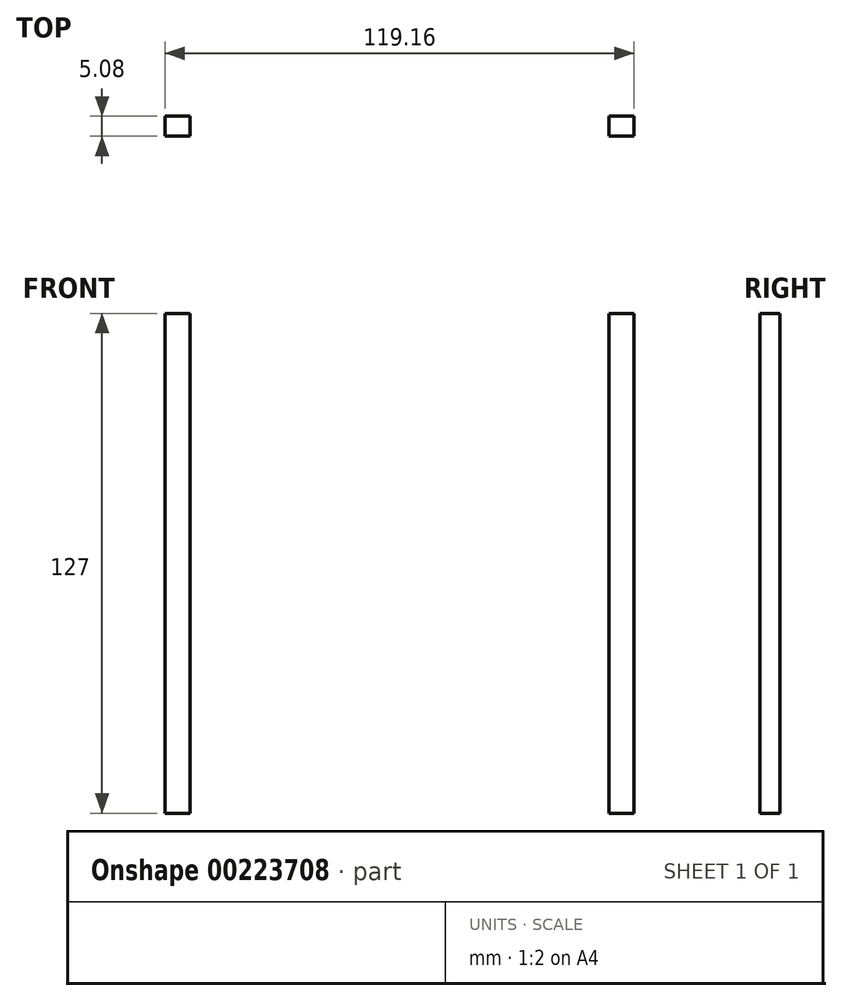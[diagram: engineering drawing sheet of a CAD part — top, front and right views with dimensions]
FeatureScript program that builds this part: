
annotation { "Feature Type Name" : "Feature", "Feature Type Description" : "" }
export const myFeature = defineFeature(function(context is Context, id is Id, definition is map)
    precondition{}
    {
        {
            var Q0;
            Q0=qCreatedBy(makeId("Front.planeOp"),FACE);
            var sketch = newSketch(context, id + "F0", { "sketchPlane" : qUnion([Q0])});
            skLineSegment(sketch, "E0.bottom", {"start": v(-59.58, 61.26) * mm, "end": v(-53.23, 61.26) * mm});
            skLineSegment(sketch, "E0.top", {"start": v(-59.58, -65.74) * mm, "end": v(-53.23, -65.74) * mm});
            skLineSegment(sketch, "E0.left", {"start": v(-59.58, 61.26) * mm, "end": v(-59.58, -65.74) * mm});
            skLineSegment(sketch, "E0.right", {"start": v(-53.23, 61.26) * mm, "end": v(-53.23, -65.74) * mm});
            skLineSegment(sketch, "E1.MirrorCS", {"start": v(59.58, 61.26) * mm, "end": v(59.58, -65.74) * mm});
            skLineSegment(sketch, "E2.MirrorCS", {"start": v(59.58, 61.26) * mm, "end": v(53.23, 61.26) * mm});
            skLineSegment(sketch, "E3.MirrorCS", {"start": v(53.23, 61.26) * mm, "end": v(53.23, -65.74) * mm});
            skLineSegment(sketch, "E4.MirrorCS", {"start": v(59.58, -65.74) * mm, "end": v(53.23, -65.74) * mm});
            skSolve(sketch);
        }
        {
            var Q0;
            Q0 = qSketchRegion(id + "F0", true);
            extrude(context, id + "F1", {"entities" : qUnion([Q0]), "depth" : 5.08 * mm});
        }
    });
